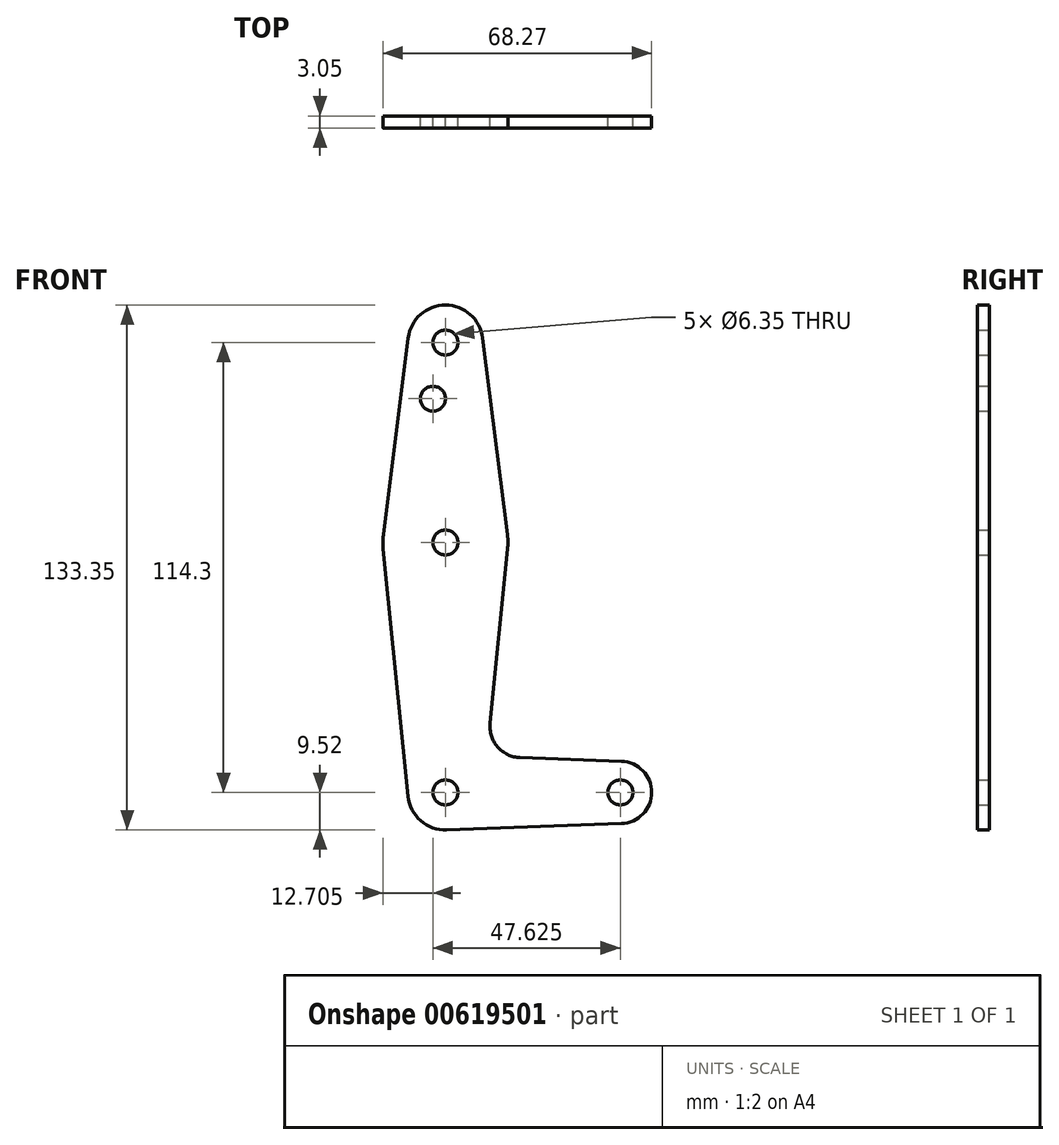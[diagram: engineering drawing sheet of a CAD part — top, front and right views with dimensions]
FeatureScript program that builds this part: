
annotation { "Feature Type Name" : "Feature", "Feature Type Description" : "" }
export const myFeature = defineFeature(function(context is Context, id is Id, definition is map)
    precondition{}
    {
        {
            var Q0;
            Q0=qCreatedBy(makeId("Front.planeOp"),FACE);
            var sketch = newSketch(context, id + "F0", { "sketchPlane" : qUnion([Q0])});
            skCircle(sketch, "E0", {"center": v(0, 0) * mm, "radius": 9.53 * mm});
            skCircle(sketch, "E1", {"center": v(0, 63.5) * mm, "radius": 15.88 * mm});
            skCircle(sketch, "E2", {"center": v(0, 114.3) * mm, "radius": 9.53 * mm});
            skCircle(sketch, "E3", {"center": v(44.45, 0) * mm, "radius": 7.94 * mm});
            skLineSegment(sketch, "E4", {"start": v(0, 114.3) * mm, "end": v(0, 63.5) * mm, "construction": true});
            skLineSegment(sketch, "E5", {"start": v(0, 0) * mm, "end": v(44.45, 0) * mm, "construction": true});
            skLineSegment(sketch, "E6", {"start": v(0, 63.5) * mm, "end": v(0, 0) * mm, "construction": true});
            skLineSegment(sketch, "E7", {"start": v(9.45, 115.5) * mm, "end": v(16.05, 63.13) * mm});
            skLineSegment(sketch, "E8", {"start": v(15.91, 63.1) * mm, "end": v(11.34, 17.6) * mm});
            skLineSegment(sketch, "E9", {"start": v(-9.48, -0.95) * mm, "end": v(-16, 64.04) * mm});
            skLineSegment(sketch, "E10", {"start": v(-15.93, 64.06) * mm, "end": v(-9.45, 115.5) * mm});
            skLineSegment(sketch, "E11", {"start": v(18.97, 8.85) * mm, "end": v(44.73, 7.93) * mm});
            skLineSegment(sketch, "E12", {"start": v(44.73, -7.93) * mm, "end": v(0, -9.53) * mm});
            skCircle(sketch, "E13", {"center": v(0, 114.3) * mm, "radius": 3.18 * mm});
            skCircle(sketch, "E14", {"center": v(0, 63.5) * mm, "radius": 3.18 * mm});
            skCircle(sketch, "E15", {"center": v(0, 0) * mm, "radius": 3.18 * mm});
            skCircle(sketch, "E16", {"center": v(44.45, 0) * mm, "radius": 3.18 * mm});
            skCircle(sketch, "E17", {"center": v(-3.17, 100.03) * mm, "radius": 3.18 * mm});
            skArc(sketch, "E18.filletArc", {"start": v(11.34, 17.6) * mm, "mid": v(13.26, 11.57) * mm, "end": v(18.97, 8.85) * mm});
            skSolve(sketch);
        }
        {
            var Q0;
            Q0=makeQuery(id+"F0.imprint","IMPRINT",FACE,{"disambiguationData":[TD([[makeQuery(id+"F0.imprint","IMPRINT",EDGE,{"derivedFrom":sQuery(id+"F0.wireOp",EDGE,"E15")}),-1.0]])]});
            var Q1;
            Q1=makeQuery(id+"F0.imprint","IMPRINT",FACE,{"disambiguationData":[TD([[makeQuery(id+"F0.imprint","IMPRINT",EDGE,{"derivedFrom":sQuery(id+"F0.wireOp",EDGE,"E13")}),-1.0]])]});
            var Q2;
            Q2=makeQuery(id+"F0.imprint","IMPRINT",FACE,{"disambiguationData":[TD([[makeQuery(id+"F0.imprint","IMPRINT",EDGE,{"derivedFrom":sQuery(id+"F0.wireOp",EDGE,"E16")}),-1.0]])]});
            var Q3;
            {var subQ0=sQuery(id+"F0.wireOp",EDGE,"E11");Q3=makeQuery(id+"F0.imprint","IMPRINT",FACE,{"disambiguationData":[TD([[makeQuery(id+"F0.imprint","IMPRINT",EDGE,{"derivedFrom":subQ0}),-1.0]])]});}
            var Q4;
            Q4=makeQuery(id+"F0.imprint","IMPRINT",FACE,{"disambiguationData":[TD([[makeQuery(id+"F0.imprint","IMPRINT",EDGE,{"derivedFrom":sQuery(id+"F0.wireOp",EDGE,"E14")}),-1.0]])]});
            var Q5;
            Q5=makeQuery(id+"F0.imprint","IMPRINT",FACE,{"disambiguationData":[TD([[makeQuery(id+"F0.imprint","IMPRINT",EDGE,{"derivedFrom":sQuery(id+"F0.wireOp",EDGE,"E17")}),-1.0]])]});
            extrude(context, id + "F1", {"entities" : qUnion([Q0, Q1, Q2, Q3, Q4, Q5]), "depth" : 3.05 * mm, "offsetDistance" : 25.4 * mm});
        }
    });
